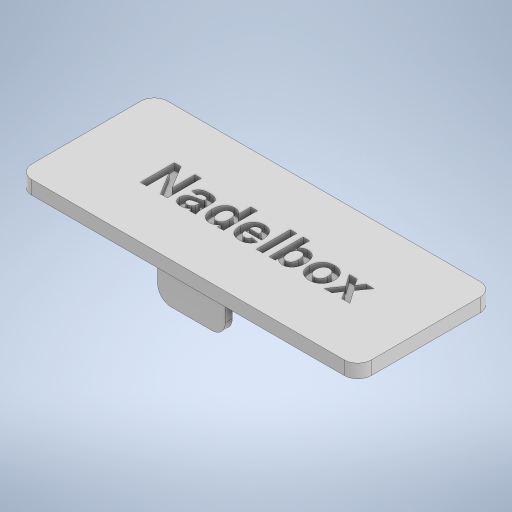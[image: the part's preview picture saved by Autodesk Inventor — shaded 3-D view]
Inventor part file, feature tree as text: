
AUTODESK INVENTOR PART (.ipt)
format: ipt  version: 2023.1 (Build 271208000, 208)  size: 451,584 bytes
history: native  units: mm
features: fillet x3, sketch x3, extrude x2, other x1
ambient origin geometry x8: Origin, YZ Plane, XZ Plane, XY Plane, X Axis, Y Axis, Z Axis, Center Point
bodies: Volumenkörper1 (feature_tree)
feature tree (9):
  extrude  "Extrusion1"  Depth=20.0mm
  extrude  "Extrusion2"  Depth=1.0mm
  fillet  "Rundung1"  Radius=2.0mm
  fillet  "Rundung2"  Radius=1.0mm
  fillet  "Rundung3"  Radius=1.0mm
  other  "Prägen1"
  sketch  "Skizze1"  dims[d0=50.0mm d1=20.0mm]
  sketch  "Skizze2"  dims[d2=10.0mm d3=25.0mm d4=2.0mm d5=0.0mm d6=1.0mm d7=1.0mm]
  sketch  "Skizze3"  dims[d8=0.5mm d9=10.0mm d10=10.0mm d11=0.5mm d12=5.0mm d13=4.5mm d14=0.0mm d15=2.0mm d16=2.0mm d17=2.0mm d18=1.0mm d19=0.0mm]
